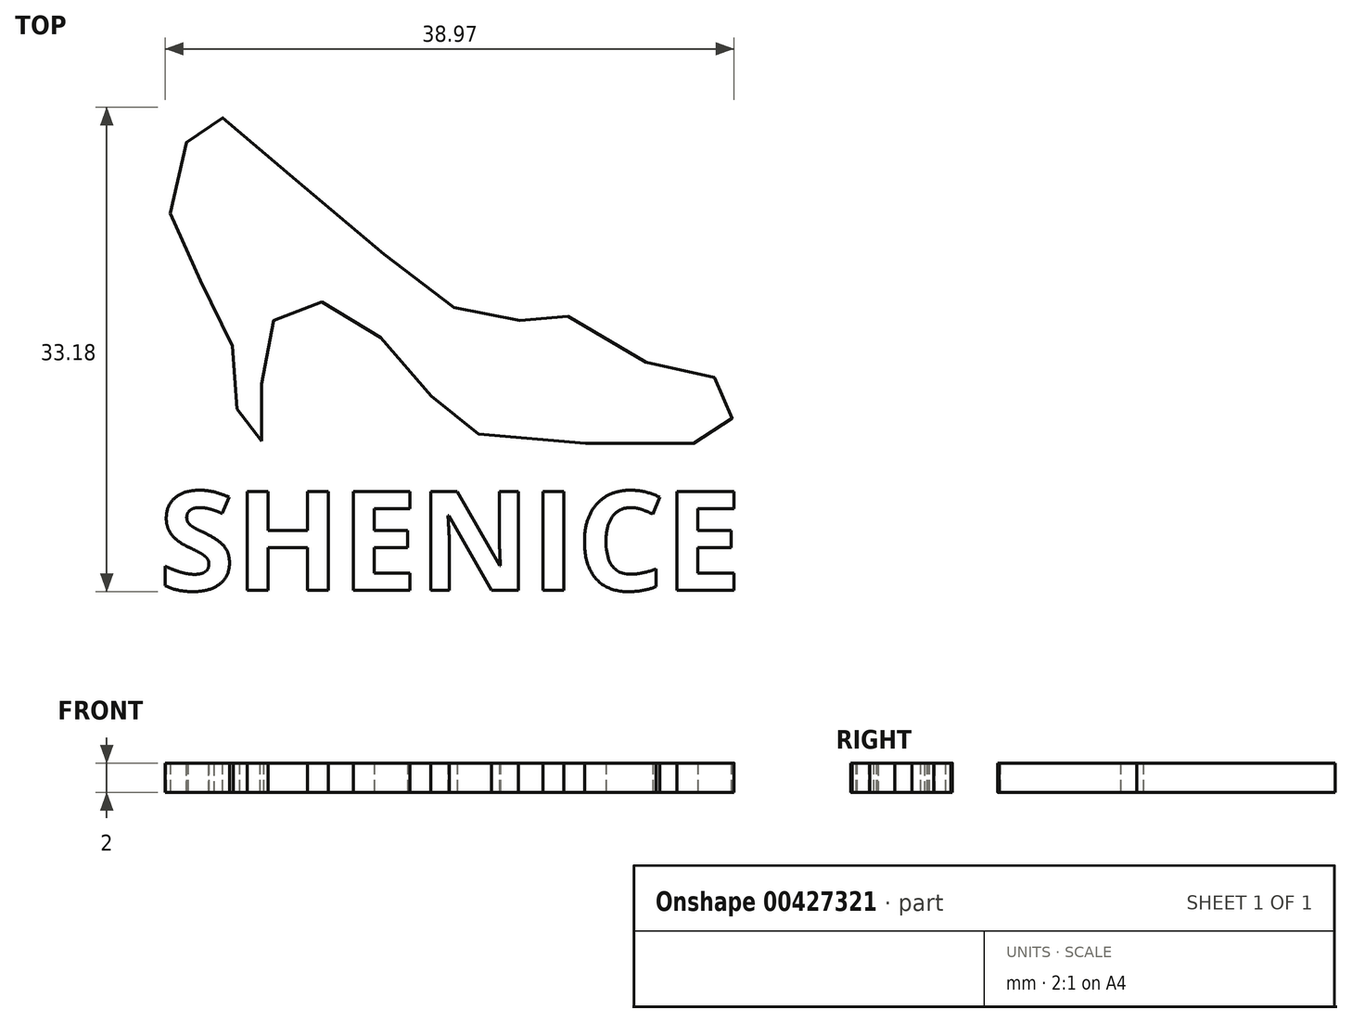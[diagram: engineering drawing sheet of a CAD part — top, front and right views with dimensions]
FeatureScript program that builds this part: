
annotation { "Feature Type Name" : "Feature", "Feature Type Description" : "" }
export const myFeature = defineFeature(function(context is Context, id is Id, definition is map)
    precondition{}
    {
        {
            var Q0;
            Q0=qCreatedBy(makeId("Top.planeOp"),FACE);
            var sketch = newSketch(context, id + "F0", { "sketchPlane" : qUnion([Q0])});
            skFitSpline(sketch, "E0", {"points": [v(7.04, 1.43) * mm, v(5.33, 1.43) * mm, v(5.4, 3.89) * mm, v(5.38, 6.46) * mm, v(4.73, 8.92) * mm, v(3.16, 12.02) * mm, v(1.14, 15.1) * mm, v(0.85, 18.27) * mm, v(1.71, 21.45) * mm, v(3.35, 24.29) * mm, v(4.31, 23.66) * mm, v(8.26, 20.24) * mm, v(14.7, 14.9) * mm, v(18.99, 11.25) * mm, v(22.02, 9.95) * mm, v(24.76, 9.7) * mm, v(27.27, 10.72) * mm, v(27.91, 10.12) * mm, v(31.73, 7.45) * mm, v(36.38, 6.14) * mm, v(38.16, 5.73) * mm, v(39.16, 4.8) * mm, v(39.36, 3.3) * mm, v(38.54, 1.96) * mm, v(37.36, 1.34) * mm, v(34.41, 1.35) * mm, v(23.83, 1.43) * mm, v(21.14, 2.32) * mm, v(19.44, 3.64) * mm, v(17.03, 6.56) * mm, v(14.6, 9.02) * mm, v(11.88, 10.65) * mm, v(10.08, 11.14) * mm, v(8.36, 10.3) * mm, v(7.3, 8.3) * mm, v(7.05, 5.44) * mm, v(6.96, 2.72) * mm, v(7.04, 1.43) * mm]});
            skSolve(sketch);
        }
        {
            var Q0;
            Q0=makeQuery(id+"F0.imprint","IMPRINT",FACE,{"disambiguationData":[TD([[makeQuery(id+"F0.imprint","IMPRINT",EDGE,{"derivedFrom":sQuery(id+"F0.wireOp",EDGE,"E0")}),-1.0]])]});
            extrude(context, id + "F1", {"entities" : qUnion([Q0]), "depth" : 2 * mm, "offsetDistance" : 25 * mm});
        }
        {
            var Q0;
            Q0=qCreatedBy(makeId("Top.planeOp"),FACE);
            var sketch = newSketch(context, id + "F2", { "sketchPlane" : qUnion([Q0])});
            skText(sketch, "E1", { "text": "SHENICE", "fontName": "OpenSans-Bold.ttf"});
            const initialGuessF2  = {"E1": [0, -0.00878, 1, 0, 0.00682]};
            skSetInitialGuess(sketch, initialGuessF2);
            skSolve(sketch);
        }
        {
            var Q0;
            Q0 = qSketchRegion(id + "F2", true);
            extrude(context, id + "F3", {"entities" : qUnion([Q0]), "depth" : 2 * mm, "offsetDistance" : 25 * mm});
        }
    });
